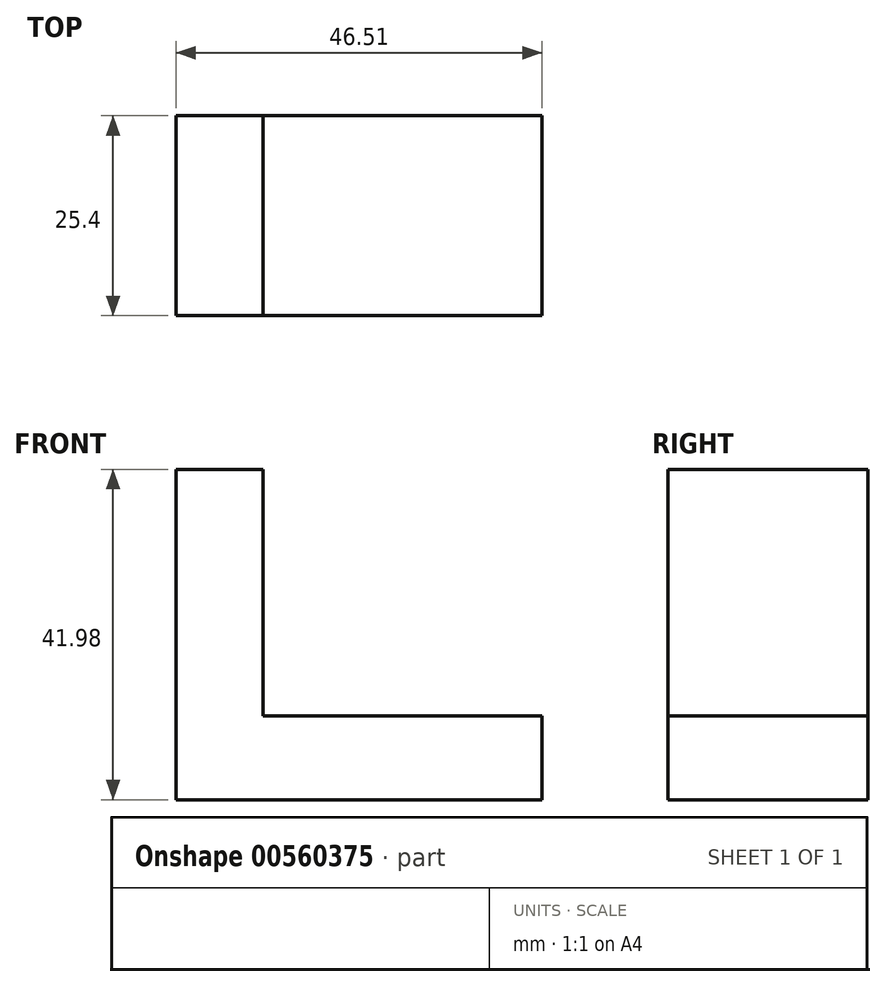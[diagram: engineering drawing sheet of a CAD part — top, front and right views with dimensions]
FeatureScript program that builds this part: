
annotation { "Feature Type Name" : "Feature", "Feature Type Description" : "" }
export const myFeature = defineFeature(function(context is Context, id is Id, definition is map)
    precondition{}
    {
        {
            var Q0;
            Q0=qCreatedBy(makeId("Front.planeOp"),FACE);
            var sketch = newSketch(context, id + "F0", { "sketchPlane" : qUnion([Q0])});
            skLineSegment(sketch, "E0", {"start": v(0, 0) * mm, "end": v(-46.5, 0) * mm});
            skLineSegment(sketch, "E1", {"start": v(-46.5, 0) * mm, "end": v(-46.5, 41.98) * mm});
            skLineSegment(sketch, "E2", {"start": v(-46.5, 41.98) * mm, "end": v(-35.47, 41.98) * mm});
            skLineSegment(sketch, "E3", {"start": v(-35.47, 41.98) * mm, "end": v(-35.47, 10.64) * mm});
            skLineSegment(sketch, "E4", {"start": v(-35.47, 10.64) * mm, "end": v(0, 10.64) * mm});
            skLineSegment(sketch, "E5", {"start": v(0, 10.64) * mm, "end": v(0, 0) * mm});
            skSolve(sketch);
        }
        {
            var Q0;
            Q0=makeQuery(id+"F0.imprint","IMPRINT",FACE,{"disambiguationData":[TD([[makeQuery(id+"F0.imprint","IMPRINT",EDGE,{"derivedFrom":sQuery(id+"F0.wireOp",EDGE,"E0")}),-1.0]])]});
            extrude(context, id + "F1", {"entities" : qUnion([Q0]), "depth" : 25.4 * mm, "offsetDistance" : 25.4 * mm});
        }
    });
